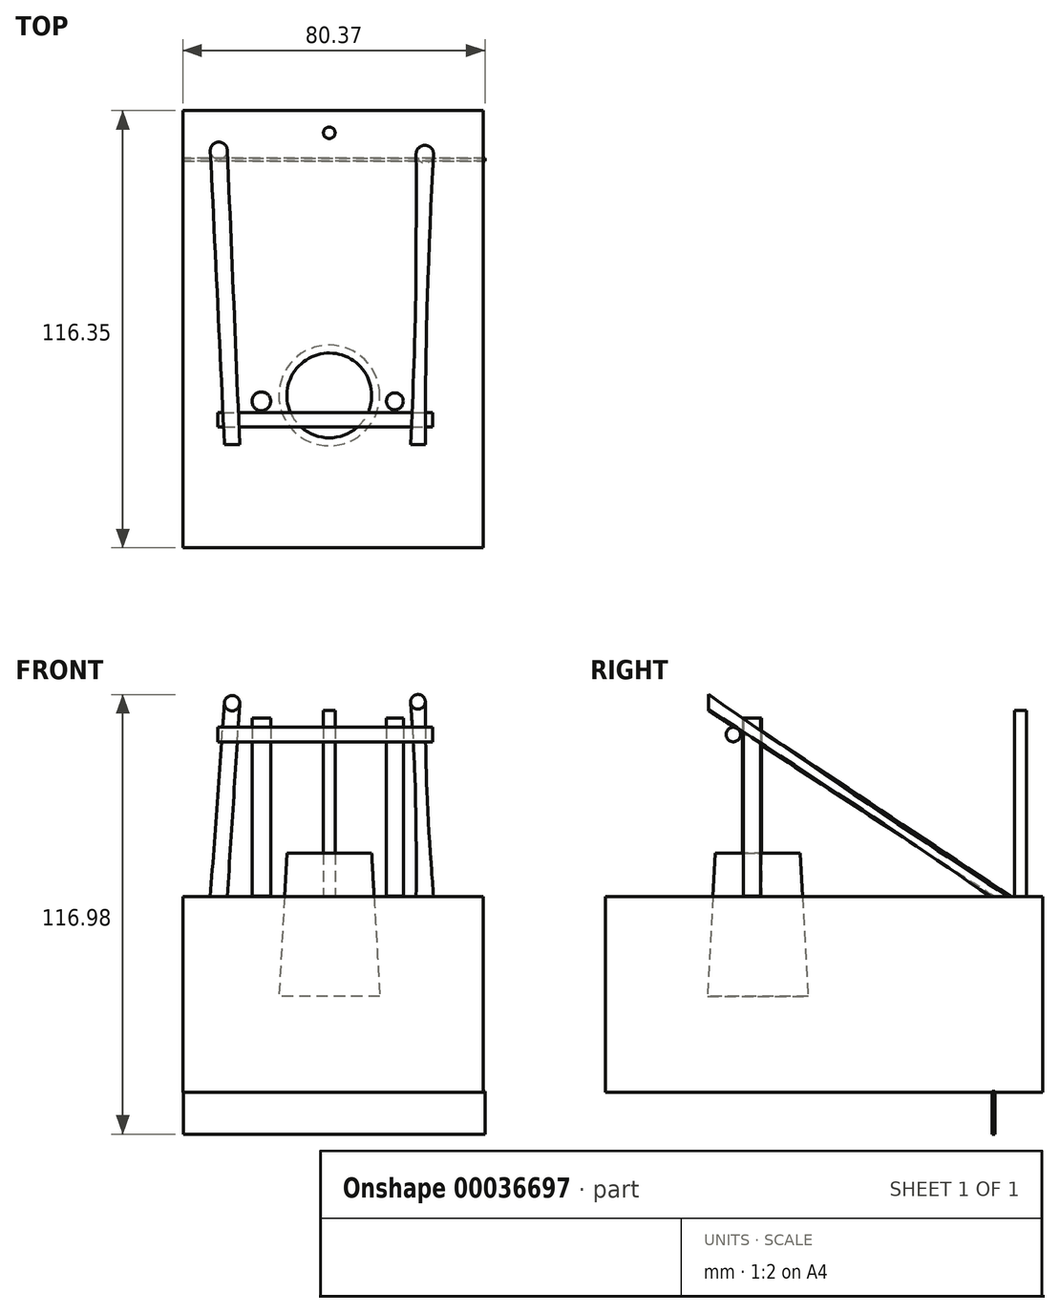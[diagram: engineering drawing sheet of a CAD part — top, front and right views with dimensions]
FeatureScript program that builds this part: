
annotation { "Feature Type Name" : "Feature", "Feature Type Description" : "" }
export const myFeature = defineFeature(function(context is Context, id is Id, definition is map)
    precondition{}
    {
        {
            var Q0;
            Q0=qCreatedBy(makeId("Front.planeOp"),FACE);
            var sketch = newSketch(context, id + "F0", { "sketchPlane" : qUnion([Q0])});
            skLineSegment(sketch, "E0.bottom", {"start": v(-38.93, 26.58) * mm, "end": v(40.95, 26.58) * mm});
            skLineSegment(sketch, "E0.top", {"start": v(-38.93, -25.5) * mm, "end": v(40.95, -25.5) * mm});
            skLineSegment(sketch, "E0.left", {"start": v(-38.93, 26.58) * mm, "end": v(-38.93, -25.5) * mm});
            skLineSegment(sketch, "E0.right", {"start": v(40.95, 26.58) * mm, "end": v(40.95, -25.5) * mm});
            skSolve(sketch);
        }
        {
            var Q0;
            Q0 = qSketchRegion(id + "F0", true);
            extrude(context, id + "F1", {"entities" : qUnion([Q0]), "depth" : 116.35 * mm});
        }
        {
            var Q0;
            Q0=qCreatedBy(makeId("Front.planeOp"),FACE);
            cPlane(context, id + "F2", {"entities" : qUnion([Q0]), "cplaneType" : CPlaneType.OFFSET, "offset" : 12.7 * mm, "width" : 152.4 * mm, "height" : 152.4 * mm});
        }
        {
            var Q0;
            Q0=qCreatedBy(makeId("Top.planeOp"),FACE);
            cPlane(context, id + "F3", {"entities" : qUnion([Q0]), "cplaneType" : CPlaneType.OFFSET, "offset" : 38.1 * mm, "width" : 152.4 * mm, "height" : 152.4 * mm});
        }
        {
            var Q0;
            Q0=qCreatedBy(id+"F3.planeOp",FACE);
            var sketch = newSketch(context, id + "F4", { "sketchPlane" : qUnion([Q0])});
            skCircle(sketch, "E1", {"center": v(0, -75.8) * mm, "radius": 11.28 * mm});
            skSolve(sketch);
        }
        {
            var Q0;
            Q0=qCreatedBy(makeId("Top.planeOp"),FACE);
            cPlane(context, id + "F5", {"entities" : qUnion([Q0]), "cplaneType" : CPlaneType.OFFSET, "offset" : 26.67 * mm, "width" : 152.4 * mm, "height" : 152.4 * mm});
        }
        {
            var Q0;
            Q0=qCreatedBy(id+"F5.planeOp",FACE);
            var sketch = newSketch(context, id + "F6", { "sketchPlane" : qUnion([Q0])});
            skCircle(sketch, "E2", {"center": v(17.44, -77.35) * mm, "radius": 2.25 * mm});
            skCircle(sketch, "E3", {"center": v(-18.07, -77.35) * mm, "radius": 2.5 * mm});
            skSolve(sketch);
        }
        {
            var Q0;
            Q0 = qSketchRegion(id + "F6", true);
            extrude(context, id + "F7", {"entities" : qUnion([Q0]), "depth" : 47.43 * mm});
        }
        {
            var Q0;
            Q0=qCreatedBy(makeId("Right.planeOp"),FACE);
            cPlane(context, id + "F8", {"entities" : qUnion([Q0]), "cplaneType" : CPlaneType.OFFSET, "offset" : 20.32 * mm, "width" : 152.4 * mm, "height" : 152.4 * mm});
        }
        {
            var Q0;
            Q0=qCreatedBy(id+"F8.planeOp",FACE);
            var sketch = newSketch(context, id + "F9", { "sketchPlane" : qUnion([Q0])});
            skCircle(sketch, "E4", {"center": v(-82.3, 69.7) * mm, "radius": 1.93 * mm});
            skSolve(sketch);
        }
        {
            var Q0;
            Q0=makeQuery(id+"F9.imprint","IMPRINT",FACE,{"disambiguationData":[TD([[makeQuery(id+"F9.imprint","IMPRINT",EDGE,{"derivedFrom":sQuery(id+"F9.wireOp",EDGE,"E4")}),1.0]])]});
            extrude(context, id + "F10", {"entities" : qUnion([Q0]), "oppositeDirection" : true, "depth" : 50 * mm, "hasSecondDirection" : true, "secondDirectionOppositeDirection" : false, "secondDirectionDepth" : 7.23 * mm});
        }
        {
            var Q0;
            Q0=qCreatedBy(id+"F2.planeOp",FACE);
            var sketch = newSketch(context, id + "F11", { "sketchPlane" : qUnion([Q0])});
            skLineSegment(sketch, "E5.bottom", {"start": v(41.44, -25.22) * mm, "end": v(-38.84, -25.22) * mm});
            skLineSegment(sketch, "E5.top", {"start": v(41.44, -36.61) * mm, "end": v(-38.84, -36.61) * mm});
            skLineSegment(sketch, "E5.left", {"start": v(41.44, -25.22) * mm, "end": v(41.44, -36.61) * mm});
            skLineSegment(sketch, "E5.right", {"start": v(-38.84, -25.22) * mm, "end": v(-38.84, -36.61) * mm});
            skSolve(sketch);
        }
        {
            var Q0;
            Q0 = qSketchRegion(id + "F11", true);
            extrude(context, id + "F12", {"entities" : qUnion([Q0]), "operationType" : NewBodyOperationType.ADD, "depth" : 0.76 * mm});
        }
        {
            var Q0;
            Q0=qCreatedBy(makeId("Top.planeOp"),FACE);
            var sketch = newSketch(context, id + "F13", { "sketchPlane" : qUnion([Q0])});
            skCircle(sketch, "E6", {"center": v(0, -75.8) * mm, "radius": 13.4 * mm});
            skSolve(sketch);
        }
        {
            var Q1;
            Q1 = qSketchRegion(id + "F13", true);
            var Q2;
            Q2=makeQuery(id+"F4.imprint","IMPRINT",FACE,{"disambiguationData":[TD([[makeQuery(id+"F4.imprint","IMPRINT",EDGE,{"derivedFrom":sQuery(id+"F4.wireOp",EDGE,"E1")}),1.0]])]});
            loft(context, id + "F14", {"sheetProfilesArray" : [{ "sheetProfileEntities" : qUnion([Q1]) }, { "sheetProfileEntities" : qUnion([Q2]) }]});
        }
        {
            var Q0;
            Q0=makeQuery(id+"F1.opExtrude","SWEPT_FACE",FACE,{"disambiguationData":[OSD([sQuery(id+"F0.wireOp",EDGE,"E0.bottom")])]});
            var sketch = newSketch(context, id + "F15", { "sketchPlane" : qUnion([Q0])});
            skCircle(sketch, "E7", {"center": v(-29.39, -10.62) * mm, "radius": 2.26 * mm});
            skSolve(sketch);
        }
        {
            var Q0;
            Q0=qCreatedBy(id+"F2.planeOp",FACE);
            cPlane(context, id + "F16", {"entities" : qUnion([Q0]), "cplaneType" : CPlaneType.OFFSET, "offset" : 76.2 * mm, "width" : 152.4 * mm, "height" : 152.4 * mm});
        }
        {
            var Q0;
            Q0=qCreatedBy(id+"F16.planeOp",FACE);
            var sketch = newSketch(context, id + "F17", { "sketchPlane" : qUnion([Q0])});
            skCircle(sketch, "E8", {"center": v(23.6, 78.41) * mm, "radius": 1.96 * mm});
            skSolve(sketch);
        }
        {
            var Q0;
            Q0=qCreatedBy(id+"F16.planeOp",FACE);
            var sketch = newSketch(context, id + "F18", { "sketchPlane" : qUnion([Q0])});
            skCircle(sketch, "E9", {"center": v(-25.85, 78.04) * mm, "radius": 2.04 * mm});
            skSolve(sketch);
        }
        {
            var Q0;
            Q0=makeQuery(id+"F18.imprint","IMPRINT",FACE,{"disambiguationData":[TD([[makeQuery(id+"F18.imprint","IMPRINT",EDGE,{"derivedFrom":sQuery(id+"F18.wireOp",EDGE,"E9")}),1.0]])]});
            var Q1;
            Q1 = qSketchRegion(id + "F15", true);
            loft(context, id + "F19", {"sheetProfilesArray" : [{ "sheetProfileEntities" : qUnion([Q0]) }, { "sheetProfileEntities" : qUnion([Q1]) }]});
        }
        {
            var Q0;
            Q0=makeQuery(id+"F1.opExtrude","SWEPT_FACE",FACE,{"disambiguationData":[OSD([sQuery(id+"F0.wireOp",EDGE,"E0.bottom")])]});
            var sketch = newSketch(context, id + "F20", { "sketchPlane" : qUnion([Q0])});
            skCircle(sketch, "E10", {"center": v(25.42, -11.57) * mm, "radius": 2.32 * mm});
            skSolve(sketch);
        }
        {
            var Q0;
            Q0 = qSketchRegion(id + "F20", true);
            var Q1;
            Q1 = qSketchRegion(id + "F17", true);
            loft(context, id + "F21", {"sheetProfilesArray" : [{ "sheetProfileEntities" : qUnion([Q0]) }, { "sheetProfileEntities" : qUnion([Q1]) }]});
        }
        {
            var Q0;
            Q0=makeQuery(id+"F1.opExtrude","SWEPT_FACE",FACE,{"disambiguationData":[OSD([sQuery(id+"F0.wireOp",EDGE,"E0.bottom")])]});
            var sketch = newSketch(context, id + "F22", { "sketchPlane" : qUnion([Q0])});
            skCircle(sketch, "E11", {"center": v(0, -5.9) * mm, "radius": 1.55 * mm});
            skSolve(sketch);
        }
        {
            var Q0;
            Q0 = qSketchRegion(id + "F22", true);
            extrude(context, id + "F23", {"entities" : qUnion([Q0]), "depth" : 49.58 * mm});
        }
    });
